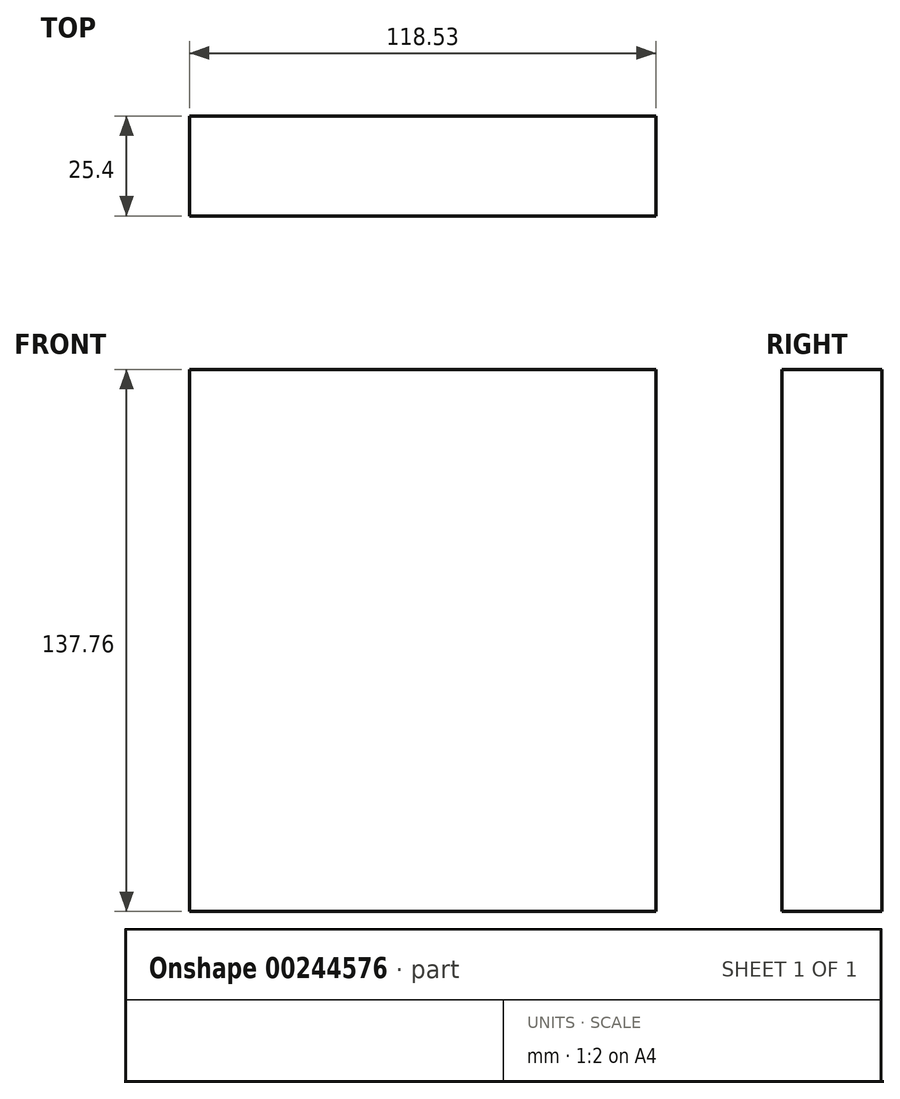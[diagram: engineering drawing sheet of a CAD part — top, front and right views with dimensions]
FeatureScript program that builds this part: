
annotation { "Feature Type Name" : "Feature", "Feature Type Description" : "" }
export const myFeature = defineFeature(function(context is Context, id is Id, definition is map)
    precondition{}
    {
        {
            var Q0;
            Q0=qCreatedBy(makeId("Front.planeOp"),FACE);
            var sketch = newSketch(context, id + "F1", { "sketchPlane" : qUnion([Q0])});
            skLineSegment(sketch, "E0.bottom", {"start": v(-60.11, 81.7) * mm, "end": v(58.42, 81.7) * mm});
            skLineSegment(sketch, "E0.top", {"start": v(-60.11, -56.05) * mm, "end": v(58.42, -56.05) * mm});
            skLineSegment(sketch, "E0.left", {"start": v(-60.11, 81.7) * mm, "end": v(-60.11, -56.05) * mm});
            skLineSegment(sketch, "E0.right", {"start": v(58.42, 81.7) * mm, "end": v(58.42, -56.05) * mm});
            skSolve(sketch);
        }
        {
            var Q0;
            Q0=makeQuery(id+"F1.imprint","IMPRINT",FACE,{"disambiguationData":[TD([[makeQuery(id+"F1.imprint","IMPRINT",EDGE,{"derivedFrom":sQuery(id+"F1.wireOp",EDGE,"E0.bottom")}),-1.0]])]});
            extrude(context, id + "F0", {"entities" : qUnion([Q0]), "depth" : 25.4 * mm});
        }
    });
